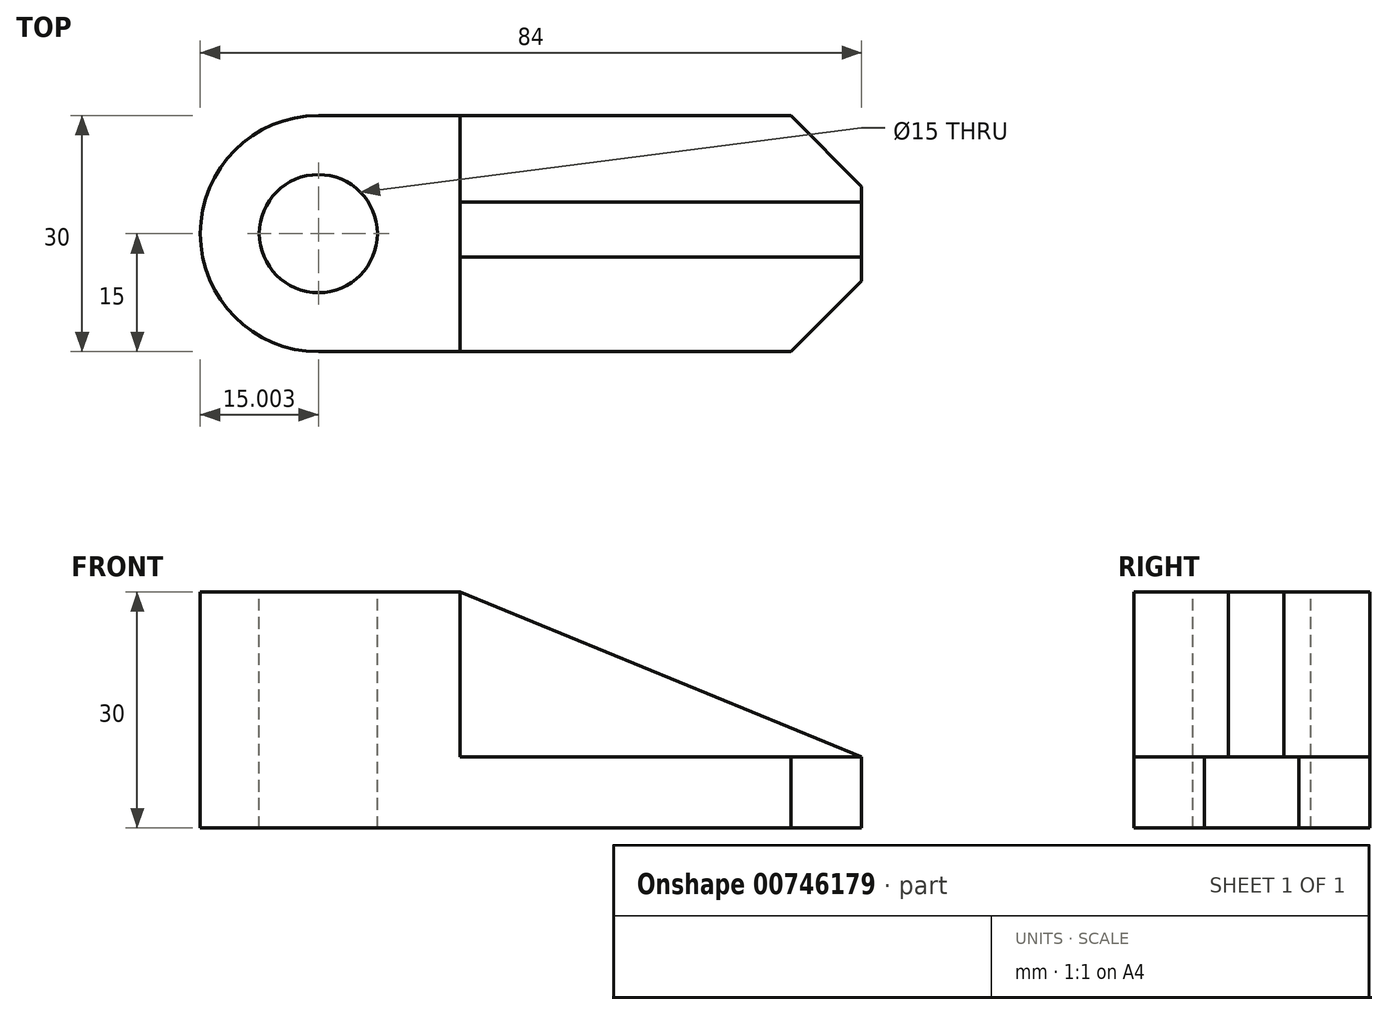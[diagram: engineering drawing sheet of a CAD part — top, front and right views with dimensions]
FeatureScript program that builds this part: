
annotation { "Feature Type Name" : "Feature", "Feature Type Description" : "" }
export const myFeature = defineFeature(function(context is Context, id is Id, definition is map)
    precondition{}
    {
        {
            var Q0;
            Q0=qCreatedBy(makeId("Top.planeOp"),FACE);
            var sketch = newSketch(context, id + "F0", { "sketchPlane" : qUnion([Q0])});
            skLineSegment(sketch, "E0", {"start": v(-15.24, 30) * mm, "end": v(44.76, 30) * mm});
            skLineSegment(sketch, "E1", {"start": v(44.76, 30) * mm, "end": v(53.76, 21) * mm});
            skLineSegment(sketch, "E2", {"start": v(53.76, 21) * mm, "end": v(53.76, 9) * mm});
            skLineSegment(sketch, "E3", {"start": v(53.76, 9) * mm, "end": v(44.76, 0) * mm});
            skLineSegment(sketch, "E4", {"start": v(-15.24, 0) * mm, "end": v(44.76, 0) * mm});
            skArc(sketch, "E5", {"start": v(-15.24, 30) * mm, "mid": v(-30.24, 15) * mm, "end": v(-15.24, 0) * mm});
            skSolve(sketch);
        }
        {
            var Q0;
            Q0 = qSketchRegion(id + "F0", true);
            extrude(context, id + "F1", {"entities" : qUnion([Q0]), "depth" : 9 * mm, "offsetDistance" : 25 * mm});
        }
        {
            var Q0;
            Q0=makeQuery(id+"F1.opExtrude","CAP_FACE",FACE,{"disambiguationData":[OSD([sQuery(id+"F0.wireOp",EDGE,"E0"),sQuery(id+"F0.wireOp",EDGE,"E1"),sQuery(id+"F0.wireOp",EDGE,"E2"),sQuery(id+"F0.wireOp",EDGE,"E3"),sQuery(id+"F0.wireOp",EDGE,"E4"),sQuery(id+"F0.wireOp",EDGE,"E5")])],"isStart":false});
            var sketch = newSketch(context, id + "F2", { "sketchPlane" : qUnion([Q0])});
            skLineSegment(sketch, "E6", {"start": v(2.76, 0) * mm, "end": v(2.76, 30) * mm});
            skSolve(sketch);
        }
        {
            var Q0;
            Q0 = qSketchRegion(id + "F2", true);
            var Q1;
            {var subQ0=sQuery(id+"F2.wireOp",EDGE,"E6");Q1=makeQuery(id+"F2.imprint","IMPRINT",FACE,{"disambiguationData":[TD([[makeQuery(id+"F2.imprint","IMPRINT",EDGE,{"derivedFrom":subQ0}),1.0]])]});}
            extrude(context, id + "F3", {"entities" : qUnion([Q0, Q1]), "operationType" : NewBodyOperationType.ADD, "depth" : 21 * mm, "offsetDistance" : 25 * mm});
        }
        {
            var Q0;
            Q0=makeQuery(id+"F3.opExtrude","CAP_FACE",FACE,{"disambiguationData":[OSD([sQuery(id+"F0.wireOp",EDGE,"E0"),sQuery(id+"F0.wireOp",EDGE,"E4"),sQuery(id+"F0.wireOp",EDGE,"E5"),sQuery(id+"F2.wireOp",EDGE,"E6")])],"isStart":false});
            var sketch = newSketch(context, id + "F4", { "sketchPlane" : qUnion([Q0])});
            skPoint(sketch, "E7.centerSnap0", {"position": v(-30.24, 15) * mm});
            skCircle(sketch, "E8", {"center": v(-15.24, 15) * mm, "radius": 7.5 * mm});
            skSolve(sketch);
        }
        {
            var Q0;
            Q0 = qSketchRegion(id + "F4", true);
            extrude(context, id + "F5", {"entities" : qUnion([Q0]), "operationType" : NewBodyOperationType.REMOVE, "oppositeDirection" : true, "depth" : 70.3 * mm, "offsetDistance" : 25 * mm});
        }
        {
            var Q0;
            Q0=makeQuery(id+"F1.opExtrude","CAP_FACE",FACE,{"disambiguationData":[OSD([sQuery(id+"F0.wireOp",EDGE,"E0"),sQuery(id+"F0.wireOp",EDGE,"E1"),sQuery(id+"F0.wireOp",EDGE,"E2"),sQuery(id+"F0.wireOp",EDGE,"E3"),sQuery(id+"F0.wireOp",EDGE,"E4"),sQuery(id+"F0.wireOp",EDGE,"E5")])],"isStart":false});
            var sketch = newSketch(context, id + "F6", { "sketchPlane" : qUnion([Q0])});
            skLineSegment(sketch, "E9", {"start": v(53.76, 12.04) * mm, "end": v(2.76, 12.04) * mm});
            skPoint(sketch, "E9.endSnap0", {"position": v(2.76, 15) * mm});
            skLineSegment(sketch, "E10", {"start": v(2.76, 12.04) * mm, "end": v(2.76, 19.04) * mm});
            skLineSegment(sketch, "E11", {"start": v(2.76, 19.04) * mm, "end": v(53.76, 19.04) * mm});
            skLineSegment(sketch, "E12", {"start": v(53.76, 19.04) * mm, "end": v(53.76, 12.04) * mm});
            skSolve(sketch);
        }
        {
            var Q0;
            Q0 = qSketchRegion(id + "F6", true);
            extrude(context, id + "F7", {"entities" : qUnion([Q0]), "operationType" : NewBodyOperationType.ADD, "depth" : 21 * mm, "offsetDistance" : 25 * mm});
        }
        {
            var Q0;
            Q0=makeQuery(id+"F7.opExtrude","SWEPT_FACE",FACE,{"disambiguationData":[OSD([sQuery(id+"F6.wireOp",EDGE,"E9")])]});
            var sketch = newSketch(context, id + "F8", { "sketchPlane" : qUnion([Q0])});
            skLineSegment(sketch, "E13", {"start": v(2.76, 30) * mm, "end": v(53.76, 9) * mm});
            skLineSegment(sketch, "E14", {"start": v(53.76, 9) * mm, "end": v(53.76, 30) * mm});
            skLineSegment(sketch, "E15", {"start": v(53.76, 30) * mm, "end": v(2.76, 30) * mm});
            skSolve(sketch);
        }
        {
            var Q0;
            Q0=makeQuery(id+"F8.imprint","IMPRINT",FACE,{"disambiguationData":[TD([[makeQuery(id+"F8.imprint","IMPRINT",EDGE,{"derivedFrom":sQuery(id+"F8.wireOp",EDGE,"E13")}),1.0]])]});
            extrude(context, id + "F9", {"entities" : qUnion([Q0]), "operationType" : NewBodyOperationType.REMOVE, "oppositeDirection" : true, "depth" : 25 * mm, "offsetDistance" : 25 * mm});
        }
    });
